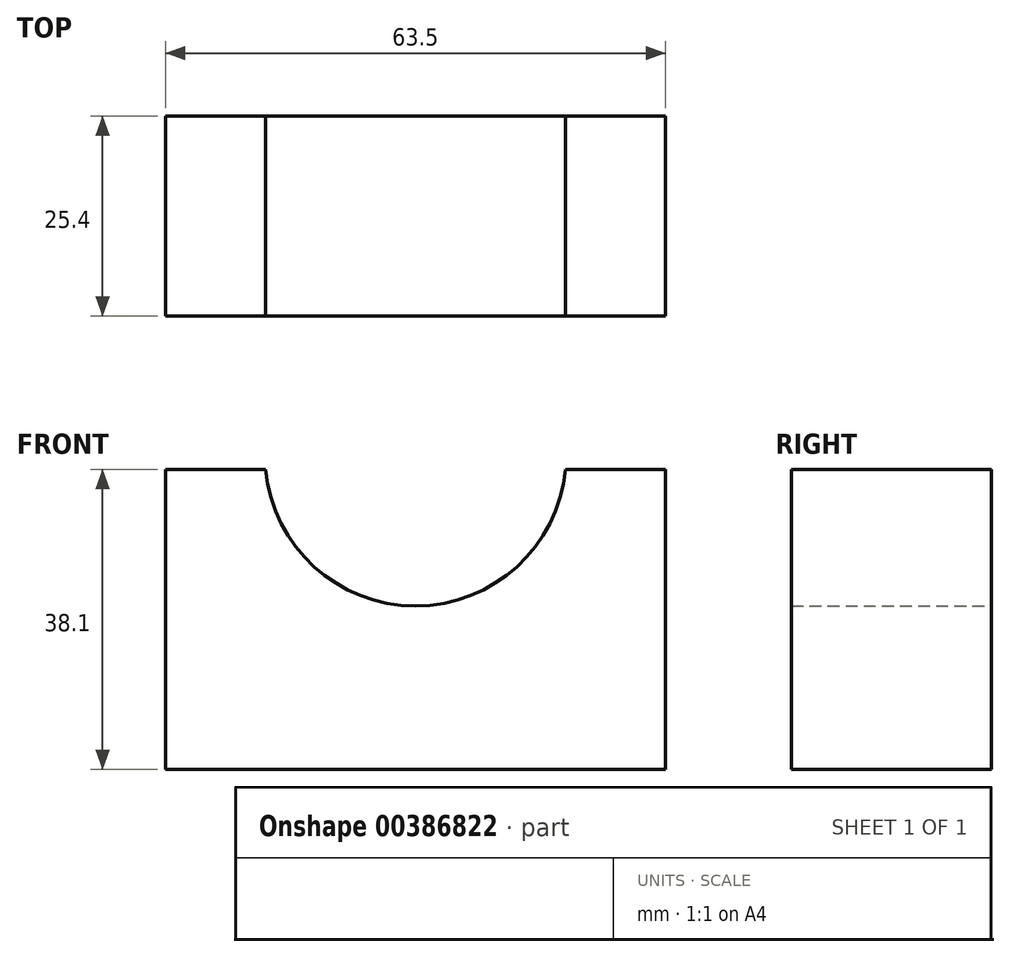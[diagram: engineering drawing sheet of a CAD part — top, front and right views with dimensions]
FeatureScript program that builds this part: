
annotation { "Feature Type Name" : "Feature", "Feature Type Description" : "" }
export const myFeature = defineFeature(function(context is Context, id is Id, definition is map)
    precondition{}
    {
        {
            var Q0;
            Q0=qCreatedBy(makeId("Front.planeOp"),FACE);
            var sketch = newSketch(context, id + "F0", { "sketchPlane" : qUnion([Q0])});
            skLineSegment(sketch, "E0", {"start": v(0, 0) * mm, "end": v(63.5, 0) * mm});
            skLineSegment(sketch, "E1", {"start": v(63.5, 0) * mm, "end": v(63.5, 38.1) * mm});
            skLineSegment(sketch, "E2", {"start": v(63.5, 38.1) * mm, "end": v(50.8, 38.1) * mm});
            skLineSegment(sketch, "E3", {"start": v(0, 0) * mm, "end": v(0, 38.1) * mm});
            skLineSegment(sketch, "E4", {"start": v(0, 38.1) * mm, "end": v(12.7, 38.1) * mm});
            skArc(sketch, "E5", {"start": v(12.7, 38.1) * mm, "mid": v(31.75, 20.77) * mm, "end": v(50.8, 38.1) * mm});
            skSolve(sketch);
        }
        {
            var Q0;
            Q0=makeQuery(id+"F0.imprint","IMPRINT",FACE,{"disambiguationData":[TD([[makeQuery(id+"F0.imprint","IMPRINT",EDGE,{"derivedFrom":sQuery(id+"F0.wireOp",EDGE,"E0")}),1.0]])]});
            extrude(context, id + "F1", {"entities" : qUnion([Q0]), "depth" : 25.4 * mm});
        }
    });
